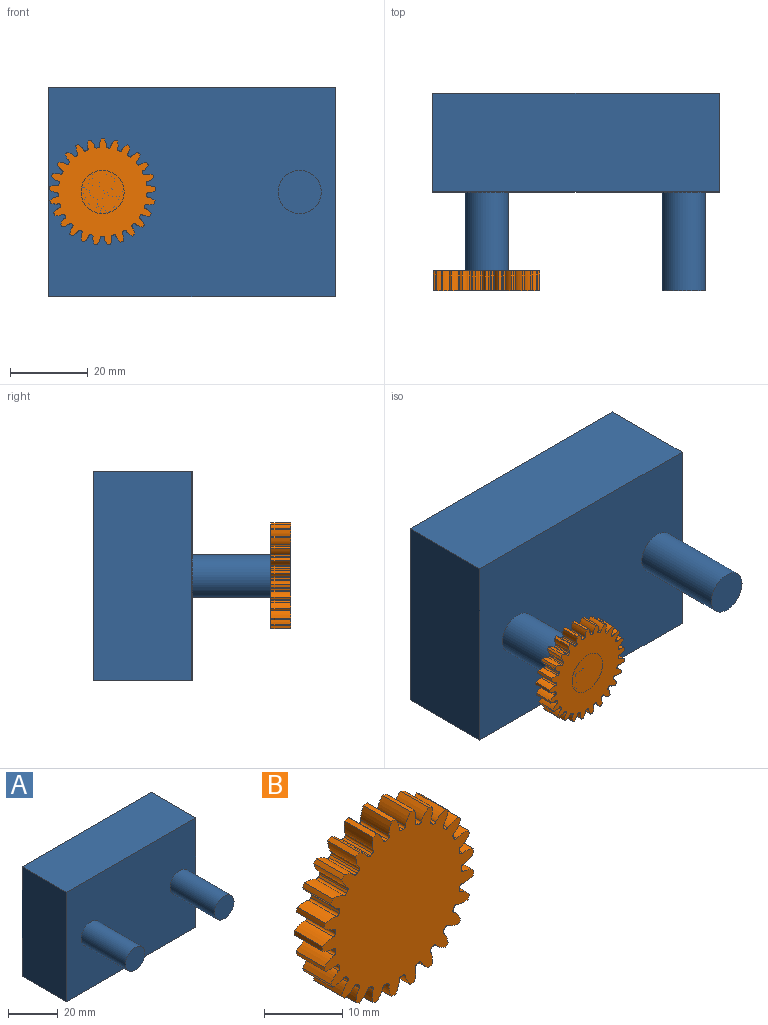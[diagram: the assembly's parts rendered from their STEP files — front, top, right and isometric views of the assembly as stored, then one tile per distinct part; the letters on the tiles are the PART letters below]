
ASSEMBLY  parts=2 mates=1
PART A: 10 faces, bbox 73.8x50.8x54 mm
  f0: plane 73.75x25.4mm, normal (0,0,1), area 1873.3mm2, adj f1,f3,f4,f5
  f1: plane 54.02x25.4mm, normal (-1,0,0), area 1372.1mm2, adj f0,f2,f4,f5
  f2: plane 73.75x25.4mm, normal (0,0,-1), area 1873.3mm2, adj f1,f3,f4,f5
  f3: plane 54.02x25.4mm, normal (1,0,0), area 1372.1mm2, adj f0,f2,f4,f5
  f4: plane 73.75x54.02mm, normal (0,-1,0), area 3789.6mm2, adj f0,f1,f2,f3,f6,f8
  f5: plane 73.75x54.02mm, normal (0,1,0), area 3984mm2, adj f0,f1,f2,f3
  f6: cylinder r=5.56mm len=25.4mm, axis (0,1,0), area 887.8mm2, adj f4,f7
  f7: plane 11.13x11.13mm, normal (0,-1,0), area 97.2mm2, adj f6
  f8: cylinder r=5.56mm len=25.4mm, axis (0,1,0), area 887.8mm2, adj f4,f9
  f9: plane 11.13x11.13mm, normal (0,-1,0), area 97.2mm2, adj f8
PART B: 152 faces, bbox 27.4x5.1x27.4 mm
  f0: extruded ~5.08x1.87mm, area 10.5mm2, adj f99,f100,f101,f102
  f1: cylinder r=11.43mm len=5.08mm, axis (0,1,0), area 2mm2, adj f100,f101,f102,f103
  f2: extruded ~5.08x1.87mm, area 10.5mm2, adj f3,f100,f101,f103
  f3: cylinder r=13.72mm len=5.08mm, axis (0,1,0), area 3.7mm2, adj f2,f4,f100,f101
  f4: extruded ~5.08x2.01mm, area 10.5mm2, adj f3,f100,f101,f104
  f5: cylinder r=11.43mm len=5.08mm, axis (0,1,0), area 2mm2, adj f100,f101,f104,f105
  f6: extruded ~5.08x1.62mm, area 10.5mm2, adj f7,f100,f101,f105
  f7: cylinder r=13.72mm len=5.08mm, axis (0,1,0), area 3.7mm2, adj f6,f8,f100,f101
  f8: extruded ~5.08x2.02mm, area 10.5mm2, adj f7,f100,f101,f106
  f9: cylinder r=11.43mm len=5.08mm, axis (0,1,0), area 2mm2, adj f100,f101,f106,f107
  f10: extruded ~5.08x1.6mm, area 10.5mm2, adj f11,f100,f101,f107
  f11: cylinder r=13.72mm len=5.08mm, axis (0,1,0), area 3.7mm2, adj f10,f12,f100,f101
  f12: extruded ~5.08x1.91mm, area 10.5mm2, adj f11,f100,f101,f108
  f13: cylinder r=11.43mm len=5.08mm, axis (0,1,0), area 2mm2, adj f100,f101,f108,f109
  f14: extruded ~5.08x1.86mm, area 10.5mm2, adj f15,f100,f101,f109
  f15: cylinder r=13.72mm len=5.08mm, axis (0,1,0), area 3.7mm2, adj f14,f16,f100,f101
  f16: extruded ~5.08x1.67mm, area 10.5mm2, adj f15,f100,f101,f110
  f17: cylinder r=11.43mm len=5.08mm, axis (0,1,0), area 2mm2, adj f100,f101,f110,f111
  f18: extruded ~5.08x2.01mm, area 10.5mm2, adj f19,f100,f101,f111
  f19: cylinder r=13.72mm len=5.08mm, axis (0,1,0), area 3.7mm2, adj f18,f20,f100,f101
  f20: extruded ~5.08x1.54mm, area 10.5mm2, adj f19,f100,f101,f112
  f21: cylinder r=11.43mm len=5.08mm, axis (0,1,0), area 2mm2, adj f100,f101,f112,f113
  f22: extruded ~5.08x2.03mm, area 10.5mm2, adj f23,f100,f101,f113
  f23: cylinder r=13.72mm len=5.08mm, axis (0,1,0), area 3.7mm2, adj f22,f24,f100,f101
  f24: extruded ~5.08x1.82mm, area 10.5mm2, adj f23,f100,f101,f114
  f25: cylinder r=11.43mm len=5.08mm, axis (0,1,0), area 2mm2, adj f100,f101,f114,f115
  f26: extruded ~5.08x1.92mm, area 10.5mm2, adj f27,f100,f101,f115
  f27: cylinder r=13.72mm len=5.08mm, axis (0,1,0), area 3.7mm2, adj f26,f28,f100,f101
  f28: extruded ~5.08x1.99mm, area 10.5mm2, adj f27,f100,f101,f116
  f29: cylinder r=11.43mm len=5.08mm, axis (0,1,0), area 2mm2, adj f100,f101,f116,f117
  f30: extruded ~5.08x1.69mm, area 10.5mm2, adj f31,f100,f101,f117
  f31: cylinder r=13.72mm len=5.08mm, axis (0,1,0), area 3.7mm2, adj f30,f32,f100,f101
  f32: extruded ~5.08x2.03mm, area 10.5mm2, adj f31,f100,f101,f118
  f33: cylinder r=11.43mm len=5.08mm, axis (0,1,0), area 2mm2, adj f100,f101,f118,f119
  f34: extruded ~5.08x1.51mm, area 10.5mm2, adj f35,f100,f101,f119
  f35: cylinder r=13.72mm len=5.08mm, axis (0,1,0), area 3.7mm2, adj f34,f36,f100,f101
  f36: extruded ~5.08x1.95mm, area 10.5mm2, adj f35,f100,f101,f120
  f37: cylinder r=11.43mm len=5.08mm, axis (0,1,0), area 2mm2, adj f100,f101,f120,f121
  f38: extruded ~5.08x1.81mm, area 10.5mm2, adj f39,f100,f101,f121
  f39: cylinder r=13.72mm len=5.08mm, axis (0,1,0), area 3.7mm2, adj f38,f40,f100,f101
  f40: extruded ~5.08x1.74mm, area 10.5mm2, adj f39,f100,f101,f122
  f41: cylinder r=11.43mm len=5.08mm, axis (0,1,0), area 2mm2, adj f100,f101,f122,f123
  f42: extruded ~5.08x1.98mm, area 10.5mm2, adj f43,f100,f101,f123
  f43: cylinder r=13.72mm len=5.08mm, axis (0,1,0), area 3.7mm2, adj f42,f44,f100,f101
  f44: extruded ~5.08x1.45mm, area 10.5mm2, adj f43,f100,f101,f124
  f45: cylinder r=11.43mm len=5.08mm, axis (0,1,0), area 2mm2, adj f100,f101,f124,f125
  f46: extruded ~5.08x2.03mm, area 10.5mm2, adj f47,f100,f101,f125
  f47: cylinder r=13.72mm len=5.08mm, axis (0,1,0), area 3.7mm2, adj f46,f48,f100,f101
  f48: extruded ~5.08x1.76mm, area 10.5mm2, adj f47,f100,f101,f126
  f49: cylinder r=11.43mm len=5.08mm, axis (0,1,0), area 2mm2, adj f100,f101,f126,f127
  f50: extruded ~5.08x1.96mm, area 10.5mm2, adj f51,f100,f101,f127
  f51: cylinder r=13.72mm len=5.08mm, axis (0,1,0), area 3.7mm2, adj f50,f52,f100,f101
  f52: extruded ~5.08x1.96mm, area 10.5mm2, adj f51,f100,f101,f128
  f53: cylinder r=11.43mm len=5.08mm, axis (0,1,0), area 2mm2, adj f100,f101,f128,f129
  f54: extruded ~5.08x1.76mm, area 10.5mm2, adj f55,f100,f101,f129
  f55: cylinder r=13.72mm len=5.08mm, axis (0,1,0), area 3.7mm2, adj f54,f56,f100,f101
  f56: extruded ~5.08x2.03mm, area 10.5mm2, adj f55,f100,f101,f130
  f57: cylinder r=11.43mm len=5.08mm, axis (0,1,0), area 2mm2, adj f100,f101,f130,f131
  f58: extruded ~5.08x1.45mm, area 10.5mm2, adj f59,f100,f101,f131
  f59: cylinder r=13.72mm len=5.08mm, axis (0,1,0), area 3.7mm2, adj f58,f60,f100,f101
  f60: extruded ~5.08x1.98mm, area 10.5mm2, adj f59,f100,f101,f132
  f61: cylinder r=11.43mm len=5.08mm, axis (0,1,0), area 2mm2, adj f100,f101,f132,f133
  f62: extruded ~5.08x1.74mm, area 10.5mm2, adj f63,f100,f101,f133
  f63: cylinder r=13.72mm len=5.08mm, axis (0,1,0), area 3.7mm2, adj f62,f64,f100,f101
  f64: extruded ~5.08x1.81mm, area 10.5mm2, adj f63,f100,f101,f134
  f65: cylinder r=11.43mm len=5.08mm, axis (0,1,0), area 2mm2, adj f100,f101,f134,f135
  f66: extruded ~5.08x1.95mm, area 10.5mm2, adj f67,f100,f101,f135
  f67: cylinder r=13.72mm len=5.08mm, axis (0,1,0), area 3.7mm2, adj f66,f68,f100,f101
  f68: extruded ~5.08x1.51mm, area 10.5mm2, adj f67,f100,f101,f136
  f69: cylinder r=11.43mm len=5.08mm, axis (0,1,0), area 2mm2, adj f100,f101,f136,f137
  f70: extruded ~5.08x2.03mm, area 10.5mm2, adj f71,f100,f101,f137
  f71: cylinder r=13.72mm len=5.08mm, axis (0,1,0), area 3.7mm2, adj f70,f72,f100,f101
  f72: extruded ~5.08x1.69mm, area 10.5mm2, adj f71,f100,f101,f138
  f73: cylinder r=11.43mm len=5.08mm, axis (0,1,0), area 2mm2, adj f100,f101,f138,f139
  f74: extruded ~5.08x1.99mm, area 10.5mm2, adj f75,f100,f101,f139
  f75: cylinder r=13.72mm len=5.08mm, axis (0,1,0), area 3.7mm2, adj f74,f76,f100,f101
  f76: extruded ~5.08x1.92mm, area 10.5mm2, adj f75,f100,f101,f140
  f77: cylinder r=11.43mm len=5.08mm, axis (0,1,0), area 2mm2, adj f100,f101,f140,f141
  f78: extruded ~5.08x1.82mm, area 10.5mm2, adj f79,f100,f101,f141
  f79: cylinder r=13.72mm len=5.08mm, axis (0,1,0), area 3.7mm2, adj f78,f80,f100,f101
  f80: extruded ~5.08x2.03mm, area 10.5mm2, adj f79,f100,f101,f142
  f81: cylinder r=11.43mm len=5.08mm, axis (0,1,0), area 2mm2, adj f100,f101,f142,f143
  f82: extruded ~5.08x1.54mm, area 10.5mm2, adj f83,f100,f101,f143
  f83: cylinder r=13.72mm len=5.08mm, axis (0,1,0), area 3.7mm2, adj f82,f84,f100,f101
  f84: extruded ~5.08x2.01mm, area 10.5mm2, adj f83,f100,f101,f144
  f85: cylinder r=11.43mm len=5.08mm, axis (0,1,0), area 2mm2, adj f100,f101,f144,f145
  f86: extruded ~5.08x1.67mm, area 10.5mm2, adj f87,f100,f101,f145
  f87: cylinder r=13.72mm len=5.08mm, axis (0,1,0), area 3.7mm2, adj f86,f88,f100,f101
  f88: extruded ~5.08x1.86mm, area 10.5mm2, adj f87,f100,f101,f146
  f89: cylinder r=11.43mm len=5.08mm, axis (0,1,0), area 2mm2, adj f100,f101,f146,f147
  f90: extruded ~5.08x1.91mm, area 10.5mm2, adj f91,f100,f101,f147
  f91: cylinder r=13.72mm len=5.08mm, axis (0,1,0), area 3.7mm2, adj f90,f92,f100,f101
  f92: extruded ~5.08x1.6mm, area 10.5mm2, adj f91,f100,f101,f148
  f93: cylinder r=11.43mm len=5.08mm, axis (0,1,0), area 2mm2, adj f100,f101,f148,f149
  f94: extruded ~5.08x2.02mm, area 10.5mm2, adj f95,f100,f101,f149
  f95: cylinder r=13.72mm len=5.08mm, axis (0,1,0), area 3.7mm2, adj f94,f96,f100,f101
  f96: extruded ~5.08x1.62mm, area 10.5mm2, adj f95,f100,f101,f150
  f97: cylinder r=11.43mm len=5.08mm, axis (0,1,0), area 2mm2, adj f100,f101,f150,f151
  f98: extruded ~5.08x2.01mm, area 10.5mm2, adj f99,f100,f101,f151
  f99: cylinder r=13.72mm len=5.08mm, axis (0,1,0), area 3.7mm2, adj f0,f98,f100,f101
  f100: plane 27.42x27.37mm, normal (0,-1,0), area 499.1mm2, adj f0,f1,f2,f3,f4,f5,f6,f7
  f101: plane 27.42x27.37mm, normal (0,1,0), area 499.1mm2, adj f0,f1,f2,f3,f4,f5,f6,f7
  f102: cylinder r=0.37mm len=5.08mm, axis (0,1,0), area 2.9mm2, adj f0,f1,f100,f101
  f103: cylinder r=0.37mm len=5.08mm, axis (0,1,0), area 2.9mm2, adj f1,f2,f100,f101
  f104: cylinder r=0.37mm len=5.08mm, axis (0,1,0), area 2.9mm2, adj f4,f5,f100,f101
  f105: cylinder r=0.37mm len=5.08mm, axis (0,1,0), area 2.9mm2, adj f5,f6,f100,f101
  f106: cylinder r=0.37mm len=5.08mm, axis (0,1,0), area 2.9mm2, adj f8,f9,f100,f101
  f107: cylinder r=0.37mm len=5.08mm, axis (0,1,0), area 2.9mm2, adj f9,f10,f100,f101
  f108: cylinder r=0.37mm len=5.08mm, axis (0,1,0), area 2.9mm2, adj f12,f13,f100,f101
  f109: cylinder r=0.37mm len=5.08mm, axis (0,1,0), area 2.9mm2, adj f13,f14,f100,f101
  f110: cylinder r=0.37mm len=5.08mm, axis (0,1,0), area 2.9mm2, adj f16,f17,f100,f101
  f111: cylinder r=0.37mm len=5.08mm, axis (0,1,0), area 2.9mm2, adj f17,f18,f100,f101
  f112: cylinder r=0.37mm len=5.08mm, axis (0,1,0), area 2.9mm2, adj f20,f21,f100,f101
  f113: cylinder r=0.37mm len=5.08mm, axis (0,1,0), area 2.9mm2, adj f21,f22,f100,f101
  f114: cylinder r=0.37mm len=5.08mm, axis (0,1,0), area 2.9mm2, adj f24,f25,f100,f101
  f115: cylinder r=0.37mm len=5.08mm, axis (0,1,0), area 2.9mm2, adj f25,f26,f100,f101
  f116: cylinder r=0.37mm len=5.08mm, axis (0,1,0), area 2.9mm2, adj f28,f29,f100,f101
  f117: cylinder r=0.37mm len=5.08mm, axis (0,1,0), area 2.9mm2, adj f29,f30,f100,f101
  f118: cylinder r=0.37mm len=5.08mm, axis (0,1,0), area 2.9mm2, adj f32,f33,f100,f101
  f119: cylinder r=0.37mm len=5.08mm, axis (0,1,0), area 2.9mm2, adj f33,f34,f100,f101
  f120: cylinder r=0.37mm len=5.08mm, axis (0,1,0), area 2.9mm2, adj f36,f37,f100,f101
  f121: cylinder r=0.37mm len=5.08mm, axis (0,1,0), area 2.9mm2, adj f37,f38,f100,f101
  f122: cylinder r=0.37mm len=5.08mm, axis (0,1,0), area 2.9mm2, adj f40,f41,f100,f101
  f123: cylinder r=0.37mm len=5.08mm, axis (0,1,0), area 2.9mm2, adj f41,f42,f100,f101
  f124: cylinder r=0.37mm len=5.08mm, axis (0,1,0), area 2.9mm2, adj f44,f45,f100,f101
  f125: cylinder r=0.37mm len=5.08mm, axis (0,1,0), area 2.9mm2, adj f45,f46,f100,f101
  f126: cylinder r=0.37mm len=5.08mm, axis (0,1,0), area 2.9mm2, adj f48,f49,f100,f101
  f127: cylinder r=0.37mm len=5.08mm, axis (0,1,0), area 2.9mm2, adj f49,f50,f100,f101
  f128: cylinder r=0.37mm len=5.08mm, axis (0,1,0), area 2.9mm2, adj f52,f53,f100,f101
  f129: cylinder r=0.37mm len=5.08mm, axis (0,1,0), area 2.9mm2, adj f53,f54,f100,f101
  f130: cylinder r=0.37mm len=5.08mm, axis (0,1,0), area 2.9mm2, adj f56,f57,f100,f101
  f131: cylinder r=0.37mm len=5.08mm, axis (0,1,0), area 2.9mm2, adj f57,f58,f100,f101
  f132: cylinder r=0.37mm len=5.08mm, axis (0,1,0), area 2.9mm2, adj f60,f61,f100,f101
  f133: cylinder r=0.37mm len=5.08mm, axis (0,1,0), area 2.9mm2, adj f61,f62,f100,f101
  f134: cylinder r=0.37mm len=5.08mm, axis (0,1,0), area 2.9mm2, adj f64,f65,f100,f101
  f135: cylinder r=0.37mm len=5.08mm, axis (0,1,0), area 2.9mm2, adj f65,f66,f100,f101
  f136: cylinder r=0.37mm len=5.08mm, axis (0,1,0), area 2.9mm2, adj f68,f69,f100,f101
  f137: cylinder r=0.37mm len=5.08mm, axis (0,1,0), area 2.9mm2, adj f69,f70,f100,f101
  f138: cylinder r=0.37mm len=5.08mm, axis (0,1,0), area 2.9mm2, adj f72,f73,f100,f101
  f139: cylinder r=0.37mm len=5.08mm, axis (0,1,0), area 2.9mm2, adj f73,f74,f100,f101
  f140: cylinder r=0.37mm len=5.08mm, axis (0,1,0), area 2.9mm2, adj f76,f77,f100,f101
  f141: cylinder r=0.37mm len=5.08mm, axis (0,1,0), area 2.9mm2, adj f77,f78,f100,f101
  f142: cylinder r=0.37mm len=5.08mm, axis (0,1,0), area 2.9mm2, adj f80,f81,f100,f101
  f143: cylinder r=0.37mm len=5.08mm, axis (0,1,0), area 2.9mm2, adj f81,f82,f100,f101
  f144: cylinder r=0.37mm len=5.08mm, axis (0,1,0), area 2.9mm2, adj f84,f85,f100,f101
  f145: cylinder r=0.37mm len=5.08mm, axis (0,1,0), area 2.9mm2, adj f85,f86,f100,f101
  f146: cylinder r=0.37mm len=5.08mm, axis (0,1,0), area 2.9mm2, adj f88,f89,f100,f101
  f147: cylinder r=0.37mm len=5.08mm, axis (0,1,0), area 2.9mm2, adj f89,f90,f100,f101
  f148: cylinder r=0.37mm len=5.08mm, axis (0,1,0), area 2.9mm2, adj f92,f93,f100,f101
  f149: cylinder r=0.37mm len=5.08mm, axis (0,1,0), area 2.9mm2, adj f93,f94,f100,f101
  f150: cylinder r=0.37mm len=5.08mm, axis (0,1,0), area 2.9mm2, adj f96,f97,f100,f101
  f151: cylinder r=0.37mm len=5.08mm, axis (0,1,0), area 2.9mm2, adj f97,f98,f100,f101
PLACE A t=(-36.49,25.4,-25.76)mm fixed
PLACE B rot(axis=(0,1,0),61.5deg) t=(-22.66,-20.32,1.25)mm
MATE revolute B.f3 <-> A.f6  axis (0,-1,0) through (-22.66,-25.4,1.25)mm
